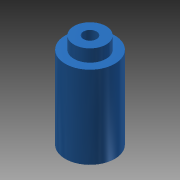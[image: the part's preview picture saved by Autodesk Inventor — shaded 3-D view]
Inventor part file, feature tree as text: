
AUTODESK INVENTOR PART (.ipt)
format: ipt  version: 2013 (Build 170138000, 138)  size: 85,504 bytes
history: native  units: mm
features: extrude x2, sketch x2
ambient origin geometry x8: Origin, YZ Plane, XZ Plane, XY Plane, X Axis, Y Axis, Z Axis, Center Point
bodies: Solid1 (feature_tree)
feature tree (4):
  extrude  "Extrusion1"  Depth=12.0mm
  extrude  "Extrusion2"  Depth=7.8mm
  sketch  "Sketch1"  dims[d0=3.2mm d1=12.0mm]
  sketch  "Sketch2"  dims[d2=20.0mm d3=0.0mm d4=7.8mm d5=3.0mm d6=0.0mm]
